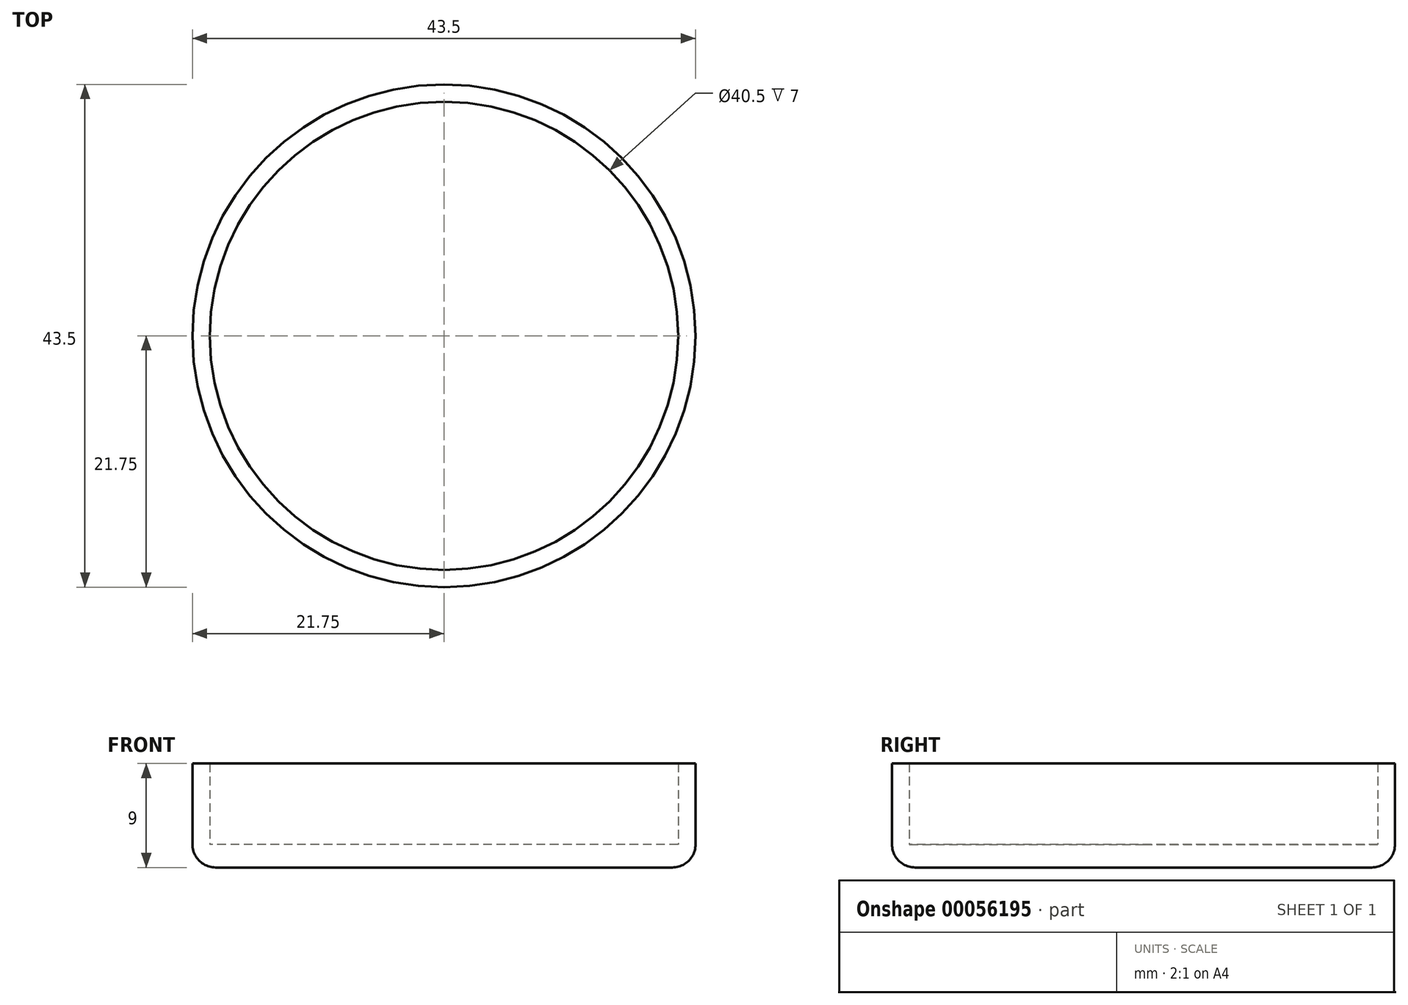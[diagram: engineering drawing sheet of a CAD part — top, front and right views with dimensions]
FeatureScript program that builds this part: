
annotation { "Feature Type Name" : "Feature", "Feature Type Description" : "" }
export const myFeature = defineFeature(function(context is Context, id is Id, definition is map)
    precondition{}
    {
        {
            var Q0;
            Q0=qCreatedBy(makeId("Top.planeOp"),FACE);
            var sketch = newSketch(context, id + "F0", { "sketchPlane" : qUnion([Q0])});
            skCircle(sketch, "E0", {"center": v(0, 0) * mm, "radius": 21.75 * mm});
            skSolve(sketch);
        }
        {
            var Q0;
            Q0 = qSketchRegion(id + "F0", true);
            extrude(context, id + "F1", {"entities" : qUnion([Q0]), "depth" : 2 * mm});
        }
        {
            var Q0;
            Q0=qCreatedBy(makeId("Top.planeOp"),FACE);
            var sketch = newSketch(context, id + "F2", { "sketchPlane" : qUnion([Q0])});
            skCircle(sketch, "E1", {"center": v(0, 0) * mm, "radius": 21.75 * mm});
            skCircle(sketch, "E2", {"center": v(0, 0) * mm, "radius": 20.25 * mm});
            skSolve(sketch);
        }
        {
            var Q0;
            Q0 = qSketchRegion(id + "F2", true);
            extrude(context, id + "F3", {"entities" : qUnion([Q0]), "operationType" : NewBodyOperationType.ADD, "depth" : 9 * mm});
        }
        {
            var Q0;
            Q0=makeQuery(id+"F1.opExtrude","CAP_EDGE",EDGE,{"disambiguationData":[OSD([sQuery(id+"F0.wireOp",EDGE,"E0")])],"isStart":true});
            fillet(context, id + "F4", {"entities" : qUnion([Q0]), "radius" : 2 * mm, "tangentPropagation" : true, "allowEdgeOverflow" : false});
        }
    });
